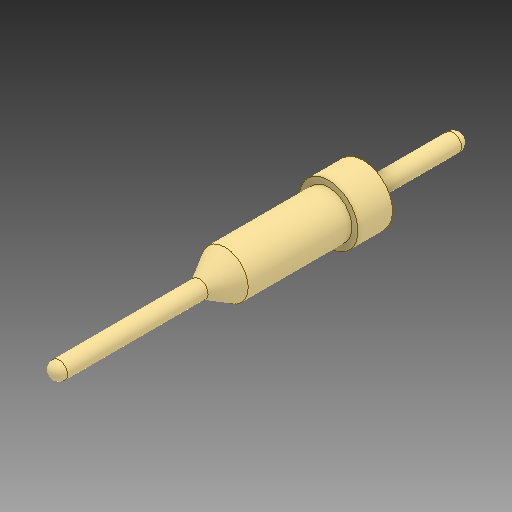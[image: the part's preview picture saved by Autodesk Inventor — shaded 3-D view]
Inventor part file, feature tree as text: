
AUTODESK INVENTOR PART (.ipt)
format: ipt  version: 2018 (Build 220112000, 112)  size: 104,960 bytes
history: native  units: mm
features: revolve x1
ambient origin geometry x8: Origin, YZ Plane, XZ Plane, XY Plane, X Axis, Y Axis, Z Axis, Center Point
bodies: Volumenkörper1 (feature_tree)
feature tree (1):
  revolve  "Revolve1"  [1 undecoded]
note: 1 required parameter value undecoded (feature->parameter linkage not recoverable at this tier; creation-order binding heuristic only, values carry confidence <= 0.55)
